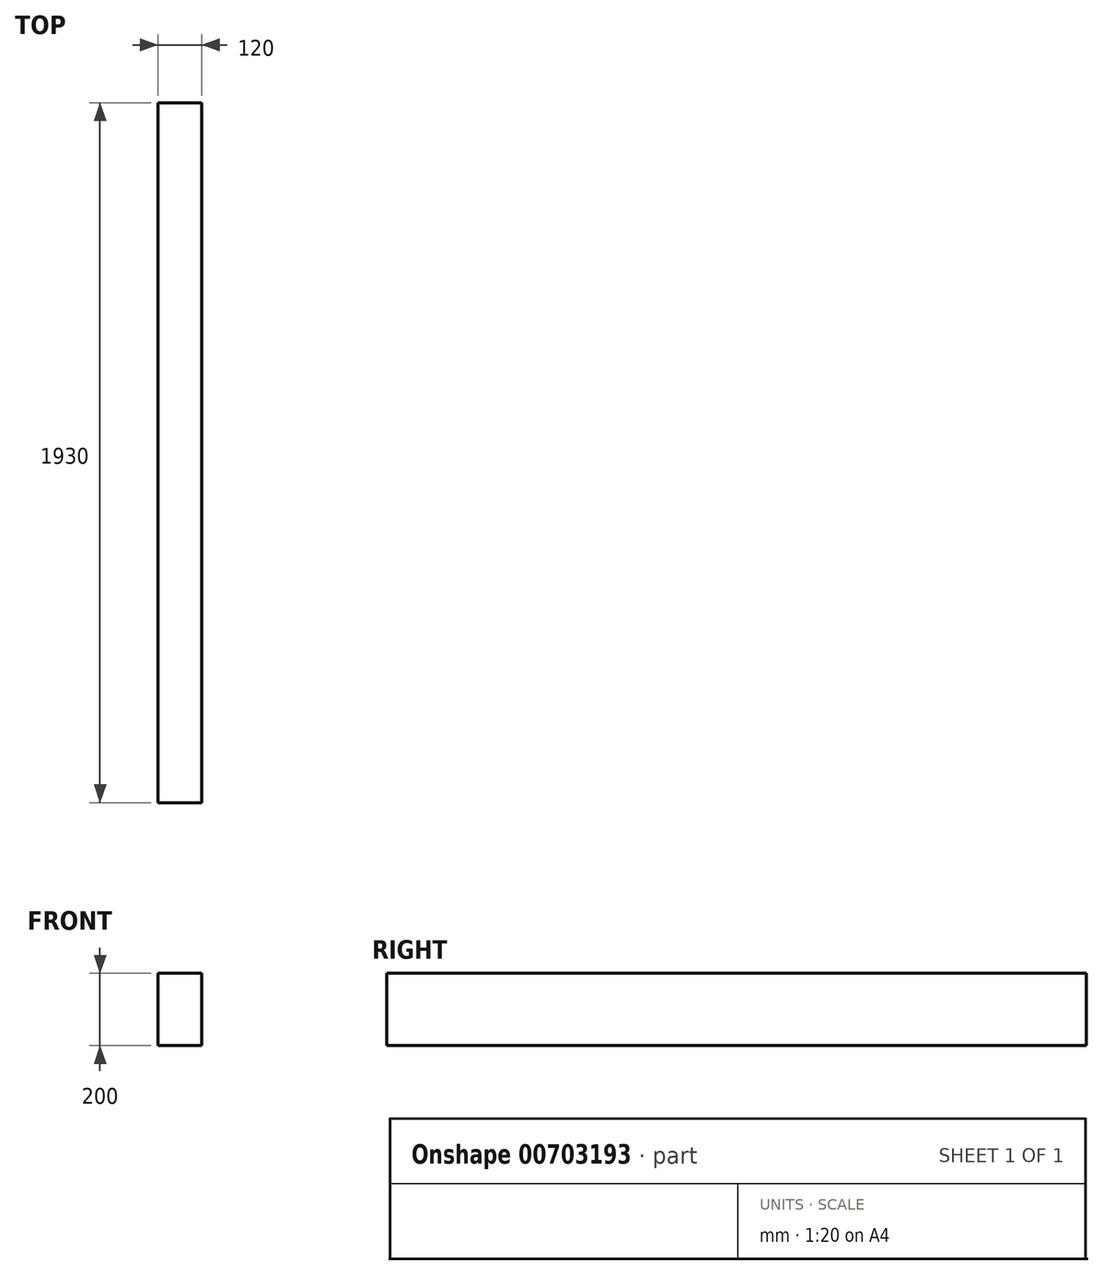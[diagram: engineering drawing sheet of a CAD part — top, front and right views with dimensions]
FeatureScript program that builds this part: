
annotation { "Feature Type Name" : "Feature", "Feature Type Description" : "" }
export const myFeature = defineFeature(function(context is Context, id is Id, definition is map)
    precondition{}
    {
        {
            var Q0;
            Q0=qCreatedBy(makeId("Front.planeOp"),FACE);
            var sketch = newSketch(context, id + "F0", { "sketchPlane" : qUnion([Q0])});
            skLineSegment(sketch, "E0.bottom", {"start": v(-61.96, 143.12) * mm, "end": v(58.04, 143.12) * mm});
            skLineSegment(sketch, "E0.top", {"start": v(-61.96, -56.88) * mm, "end": v(58.04, -56.88) * mm});
            skLineSegment(sketch, "E0.left", {"start": v(-61.96, 143.12) * mm, "end": v(-61.96, -56.88) * mm});
            skLineSegment(sketch, "E0.right", {"start": v(58.04, 143.12) * mm, "end": v(58.04, -56.88) * mm});
            skSolve(sketch);
        }
        {
            var Q0;
            Q0=makeQuery(id+"F0.imprint","IMPRINT",FACE,{"disambiguationData":[TD([[makeQuery(id+"F0.imprint","IMPRINT",EDGE,{"derivedFrom":sQuery(id+"F0.wireOp",EDGE,"E0.bottom")}),-1.0]])]});
            extrude(context, id + "F1", {"entities" : qUnion([Q0]), "depth" : 1930 * mm, "offsetDistance" : 25 * mm});
        }
    });
